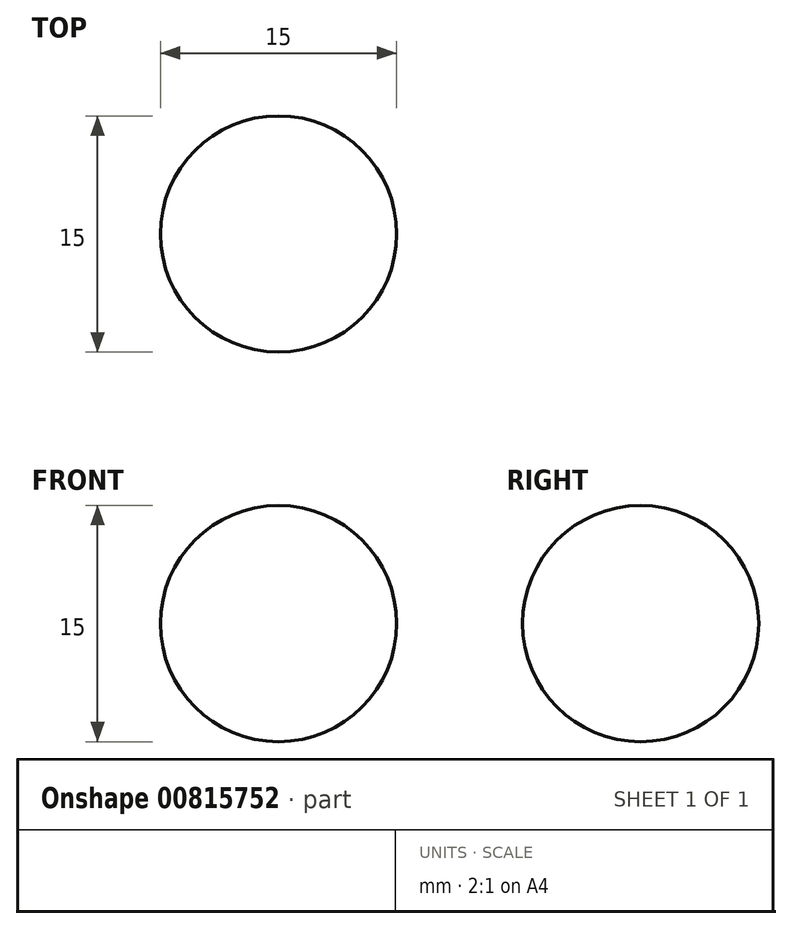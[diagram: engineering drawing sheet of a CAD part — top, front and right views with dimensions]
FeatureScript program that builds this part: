
annotation { "Feature Type Name" : "Feature", "Feature Type Description" : "" }
export const myFeature = defineFeature(function(context is Context, id is Id, definition is map)
    precondition{}
    {
        {
            var Q0;
            Q0=qCreatedBy(makeId("Front.planeOp"),FACE);
            var sketch = newSketch(context, id + "F0", { "sketchPlane" : qUnion([Q0])});
            skArc(sketch, "E0", {"start": v(0, -7.5) * mm, "mid": v(7.5, 0) * mm, "end": v(0, 7.5) * mm});
            skLineSegment(sketch, "E1", {"start": v(0, -7.5) * mm, "end": v(0, 7.5) * mm});
            skSolve(sketch);
        }
        {
            var Q0;
            Q0=makeQuery(id+"F0.imprint","IMPRINT",FACE,{"disambiguationData":[TD([[makeQuery(id+"F0.imprint","IMPRINT",EDGE,{"derivedFrom":sQuery(id+"F0.wireOp",EDGE,"E0")}),1.0]])]});
            var Q1;
            Q1=sQuery(id+"F0.wireOp",EDGE,"E1");
            revolve(context, id + "F1", {"surfaceOperationType" : NewSurfaceOperationType.NEW, "entities" : qUnion([Q0]), "axis" : qUnion([Q1]), "revolveType" : RevolveType.FULL});
        }
    });
